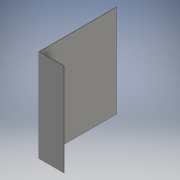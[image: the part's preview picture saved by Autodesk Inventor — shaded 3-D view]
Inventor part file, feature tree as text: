
AUTODESK INVENTOR PART (.ipt)
format: ipt  version: 2016 SP1 (Build 200210100, 210)  size: 89,600 bytes
history: native  units: mm
features: extrude x1, sketch x1
ambient origin geometry x8: Origin, YZ Plane, XZ Plane, XY Plane, X Axis, Y Axis, Z Axis, Center Point
bodies: Solid1 (feature_tree)
feature tree (2):
  extrude  "Extrusion1"  Depth=1.0mm
  sketch  "Sketch1"  dims[d0=250.0mm d1=1.0mm d2=249.0mm d3=80.0mm d4=300.0mm d5=0.0mm]
